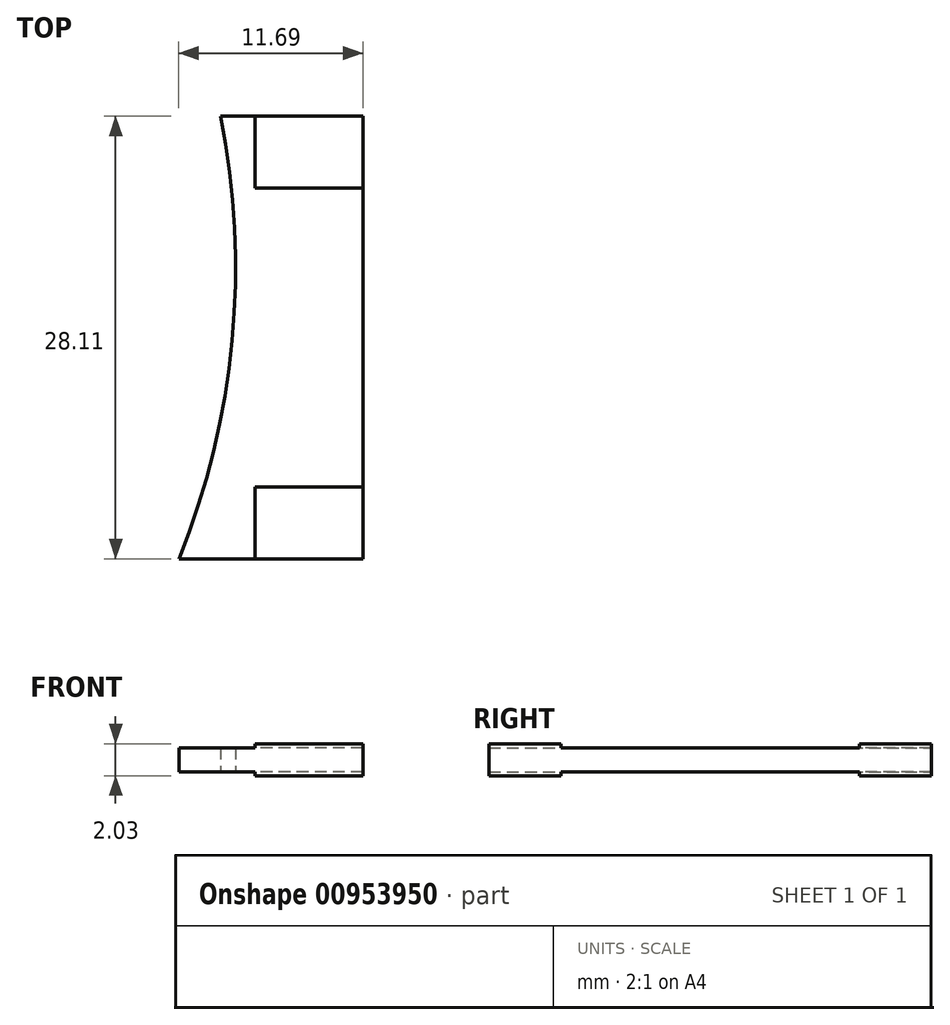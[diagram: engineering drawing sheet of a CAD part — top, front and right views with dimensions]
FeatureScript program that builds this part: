
annotation { "Feature Type Name" : "Feature", "Feature Type Description" : "" }
export const myFeature = defineFeature(function(context is Context, id is Id, definition is map)
    precondition{}
    {
        {
            var Q0;
            Q0=qCreatedBy(makeId("Top.planeOp"),FACE);
            var sketch = newSketch(context, id + "F0", { "sketchPlane" : qUnion([Q0])});
            skLineSegment(sketch, "E0", {"start": v(-53.37, 5.28) * mm, "end": v(-53.37, -22.83) * mm});
            skLineSegment(sketch, "E1", {"start": v(-53.37, -22.83) * mm, "end": v(-65.06, -22.83) * mm});
            skLineSegment(sketch, "E2", {"start": v(-53.37, 5.28) * mm, "end": v(-62.41, 5.28) * mm});
            skArc(sketch, "E3", {"start": v(-65.06, -22.83) * mm, "mid": v(-61.67, -8.97) * mm, "end": v(-62.41, 5.28) * mm});
            skSolve(sketch);
        }
        {
            var Q0;
            Q0=makeQuery(id+"F0.imprint","IMPRINT",FACE,{"disambiguationData":[TD([[makeQuery(id+"F0.imprint","IMPRINT",EDGE,{"derivedFrom":sQuery(id+"F0.wireOp",EDGE,"E0")}),-1.0]])]});
            extrude(context, id + "F1", {"entities" : qUnion([Q0]), "depth" : 1.52 * mm, "offsetDistance" : 25.4 * mm});
        }
        {
            var Q0;
            Q0=makeQuery(id+"F1.opExtrude","CAP_FACE",FACE,{"disambiguationData":[OSD([sQuery(id+"F0.wireOp",EDGE,"E0"),sQuery(id+"F0.wireOp",EDGE,"E1"),sQuery(id+"F0.wireOp",EDGE,"E2"),sQuery(id+"F0.wireOp",EDGE,"E3")])],"isStart":false});
            var sketch = newSketch(context, id + "F2", { "sketchPlane" : qUnion([Q0])});
            skLineSegment(sketch, "E4.bottom", {"start": v(-53.37, 5.28) * mm, "end": v(-60.23, 5.28) * mm});
            skLineSegment(sketch, "E4.top", {"start": v(-53.37, 0.7) * mm, "end": v(-60.23, 0.7) * mm});
            skLineSegment(sketch, "E4.left", {"start": v(-53.37, 5.28) * mm, "end": v(-53.37, 0.7) * mm});
            skLineSegment(sketch, "E4.right", {"start": v(-60.23, 5.28) * mm, "end": v(-60.23, 0.7) * mm});
            skLineSegment(sketch, "E5.bottom", {"start": v(-53.37, -22.83) * mm, "end": v(-60.23, -22.83) * mm});
            skLineSegment(sketch, "E5.top", {"start": v(-53.37, -18.26) * mm, "end": v(-60.23, -18.26) * mm});
            skLineSegment(sketch, "E5.left", {"start": v(-53.37, -22.83) * mm, "end": v(-53.37, -18.26) * mm});
            skLineSegment(sketch, "E5.right", {"start": v(-60.23, -22.83) * mm, "end": v(-60.23, -18.26) * mm});
            skSolve(sketch);
        }
        {
            var Q0;
            Q0=makeQuery(id+"F2.imprint","IMPRINT",FACE,{"disambiguationData":[TD([[makeQuery(id+"F2.imprint","IMPRINT",EDGE,{"derivedFrom":sQuery(id+"F2.wireOp",EDGE,"E4.bottom")}),1.0]])]});
            var Q1;
            Q1=makeQuery(id+"F2.imprint","IMPRINT",FACE,{"disambiguationData":[TD([[makeQuery(id+"F2.imprint","IMPRINT",EDGE,{"derivedFrom":sQuery(id+"F2.wireOp",EDGE,"E5.bottom")}),-1.0]])]});
            extrude(context, id + "F3", {"entities" : qUnion([Q0, Q1]), "operationType" : NewBodyOperationType.ADD, "depth" : 0.25 * mm, "offsetDistance" : 25.4 * mm});
        }
        {
            var Q0;
            Q0=makeQuery(id+"F1.opExtrude","CAP_FACE",FACE,{"disambiguationData":[OSD([sQuery(id+"F0.wireOp",EDGE,"E0"),sQuery(id+"F0.wireOp",EDGE,"E1"),sQuery(id+"F0.wireOp",EDGE,"E2"),sQuery(id+"F0.wireOp",EDGE,"E3")])],"isStart":true});
            var sketch = newSketch(context, id + "F4", { "sketchPlane" : qUnion([Q0])});
            skLineSegment(sketch, "E6.bottom", {"start": v(-53.37, -5.28) * mm, "end": v(-60.23, -5.28) * mm});
            skLineSegment(sketch, "E6.top", {"start": v(-53.37, -0.7) * mm, "end": v(-60.23, -0.7) * mm});
            skLineSegment(sketch, "E6.left", {"start": v(-53.37, -5.28) * mm, "end": v(-53.37, -0.7) * mm});
            skLineSegment(sketch, "E6.right", {"start": v(-60.23, -5.28) * mm, "end": v(-60.23, -0.7) * mm});
            skLineSegment(sketch, "E7.bottom", {"start": v(-53.37, 22.83) * mm, "end": v(-60.23, 22.83) * mm});
            skLineSegment(sketch, "E7.top", {"start": v(-53.37, 18.26) * mm, "end": v(-60.23, 18.26) * mm});
            skLineSegment(sketch, "E7.left", {"start": v(-53.37, 22.83) * mm, "end": v(-53.37, 18.26) * mm});
            skLineSegment(sketch, "E7.right", {"start": v(-60.23, 22.83) * mm, "end": v(-60.23, 18.26) * mm});
            skSolve(sketch);
        }
        {
            var Q0;
            Q0=makeQuery(id+"F4.imprint","IMPRINT",FACE,{"disambiguationData":[TD([[makeQuery(id+"F4.imprint","IMPRINT",EDGE,{"derivedFrom":sQuery(id+"F4.wireOp",EDGE,"E6.bottom")}),-1.0]])]});
            var Q1;
            Q1=makeQuery(id+"F4.imprint","IMPRINT",FACE,{"disambiguationData":[TD([[makeQuery(id+"F4.imprint","IMPRINT",EDGE,{"derivedFrom":sQuery(id+"F4.wireOp",EDGE,"E7.bottom")}),1.0]])]});
            extrude(context, id + "F5", {"entities" : qUnion([Q0, Q1]), "operationType" : NewBodyOperationType.ADD, "depth" : 0.25 * mm, "offsetDistance" : 25.4 * mm});
        }
    });
